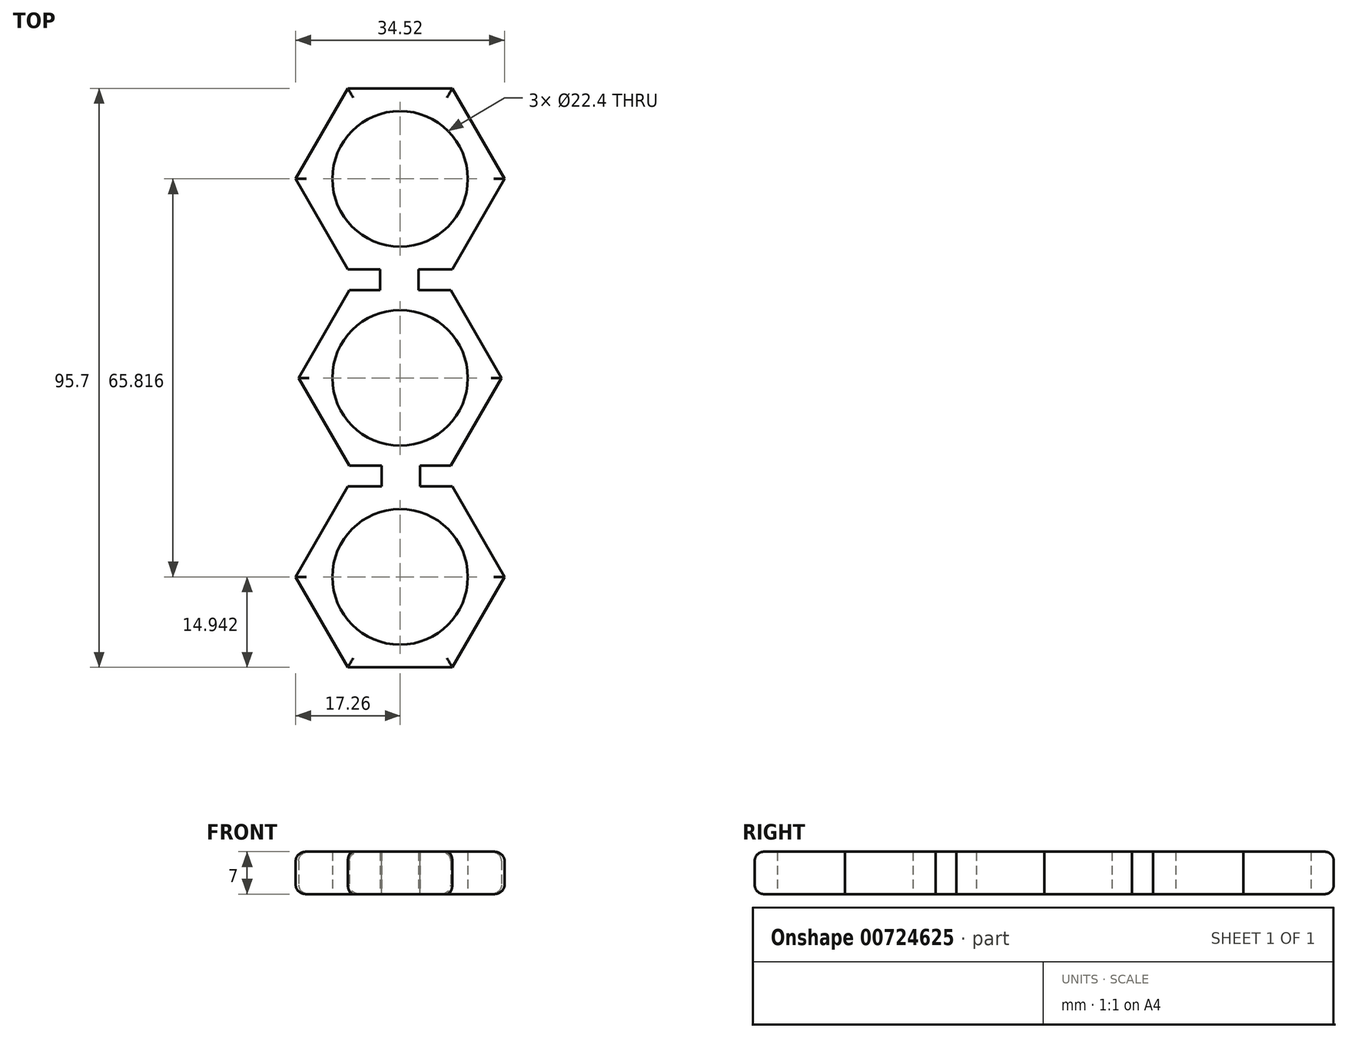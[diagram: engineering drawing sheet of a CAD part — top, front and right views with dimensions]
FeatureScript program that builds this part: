
annotation { "Feature Type Name" : "Feature", "Feature Type Description" : "" }
export const myFeature = defineFeature(function(context is Context, id is Id, definition is map)
    precondition{}
    {
        {
            var Q0;
            Q0=qCreatedBy(makeId("Top.planeOp"),FACE);
            var sketch = newSketch(context, id + "F0", { "sketchPlane" : qUnion([Q0])});
            skCircle(sketch, "E0", {"center": v(0, 0) * mm, "radius": 11.2 * mm});
            skLineSegment(sketch, "E1.0", {"start": v(8.38, -14.51) * mm, "end": v(-8.38, -14.51) * mm});
            skLineSegment(sketch, "E1.1", {"start": v(-8.38, -14.51) * mm, "end": v(-16.76, 0) * mm});
            skLineSegment(sketch, "E1.2", {"start": v(-16.76, 0) * mm, "end": v(-8.38, 14.51) * mm});
            skLineSegment(sketch, "E1.3", {"start": v(-8.38, 14.51) * mm, "end": v(8.38, 14.51) * mm});
            skLineSegment(sketch, "E1.4", {"start": v(8.38, 14.51) * mm, "end": v(16.76, 0) * mm});
            skLineSegment(sketch, "E1.5", {"start": v(16.76, 0) * mm, "end": v(8.38, -14.51) * mm});
            skPoint(sketch, "E1.0.midPoint", {"position": v(0, -14.51) * mm});
            skCircle(sketch, "E2", {"center": v(0, 32.9) * mm, "radius": 11.2 * mm});
            skLineSegment(sketch, "E3.0", {"start": v(8.63, 17.96) * mm, "end": v(-8.63, 17.96) * mm});
            skLineSegment(sketch, "E3.1", {"start": v(-8.63, 17.96) * mm, "end": v(-17.26, 32.9) * mm});
            skLineSegment(sketch, "E3.2", {"start": v(-17.26, 32.9) * mm, "end": v(-8.63, 47.85) * mm});
            skLineSegment(sketch, "E3.3", {"start": v(-8.63, 47.85) * mm, "end": v(8.63, 47.85) * mm});
            skLineSegment(sketch, "E3.4", {"start": v(8.63, 47.85) * mm, "end": v(17.26, 32.9) * mm});
            skLineSegment(sketch, "E3.5", {"start": v(17.26, 32.9) * mm, "end": v(8.63, 17.96) * mm});
            skPoint(sketch, "E3.0.midPoint", {"position": v(0, 17.96) * mm});
            skCircle(sketch, "E4.1.0", {"center": v(0, -32.9) * mm, "radius": 11.2 * mm});
            skLineSegment(sketch, "E4.1.1", {"start": v(-8.63, -47.85) * mm, "end": v(-17.26, -32.9) * mm});
            skLineSegment(sketch, "E4.1.2", {"start": v(17.26, -32.9) * mm, "end": v(8.63, -47.85) * mm});
            skLineSegment(sketch, "E4.1.3", {"start": v(8.63, -17.96) * mm, "end": v(17.26, -32.9) * mm});
            skLineSegment(sketch, "E4.1.4", {"start": v(-8.63, -17.96) * mm, "end": v(8.63, -17.96) * mm});
            skLineSegment(sketch, "E4.1.5", {"start": v(-17.26, -32.9) * mm, "end": v(-8.63, -17.96) * mm});
            skLineSegment(sketch, "E4.1.6", {"start": v(8.63, -47.85) * mm, "end": v(-8.63, -47.85) * mm});
            skLineSegment(sketch, "E5", {"start": v(-3.3, 17.96) * mm, "end": v(-3.3, 14.51) * mm});
            skLineSegment(sketch, "E6", {"start": v(3.02, 17.96) * mm, "end": v(3.02, 14.51) * mm});
            skLineSegment(sketch, "E7.1.0", {"start": v(3.3, -17.96) * mm, "end": v(3.3, -14.51) * mm});
            skLineSegment(sketch, "E7.1.1", {"start": v(-3.02, -17.96) * mm, "end": v(-3.02, -14.51) * mm});
            skSolve(sketch);
        }
        {
            var Q0;
            Q0=makeQuery(id+"F0.imprint","IMPRINT",FACE,{"disambiguationData":[TD([[makeQuery(id+"F0.imprint","IMPRINT",EDGE,{"derivedFrom":sQuery(id+"F0.wireOp",EDGE,"E2")}),-1.0]])]});
            var Q1;
            Q1=makeQuery(id+"F0.imprint","IMPRINT",FACE,{"disambiguationData":[TD([[makeQuery(id+"F0.imprint","IMPRINT",EDGE,{"derivedFrom":sQuery(id+"F0.wireOp",EDGE,"E0")}),-1.0]])]});
            var Q2;
            {var subQ0=sQuery(id+"F0.wireOp",EDGE,"E5");Q2=makeQuery(id+"F0.imprint","IMPRINT",FACE,{"disambiguationData":[TD([[makeQuery(id+"F0.imprint","IMPRINT",EDGE,{"derivedFrom":subQ0}),1.0]])]});}
            var Q3;
            Q3=makeQuery(id+"F0.imprint","IMPRINT",FACE,{"disambiguationData":[TD([[makeQuery(id+"F0.imprint","IMPRINT",EDGE,{"derivedFrom":sQuery(id+"F0.wireOp",EDGE,"E4.1.0")}),-1.0]])]});
            var Q4;
            {var subQ0=sQuery(id+"F0.wireOp",EDGE,"E7.1.0");Q4=makeQuery(id+"F0.imprint","IMPRINT",FACE,{"disambiguationData":[TD([[makeQuery(id+"F0.imprint","IMPRINT",EDGE,{"derivedFrom":subQ0}),1.0]])]});}
            extrude(context, id + "F1", {"entities" : qUnion([Q0, Q1, Q2, Q3, Q4]), "depth" : 7 * mm, "offsetDistance" : 25 * mm});
        }
        {
            var Q0;
            Q0=makeQuery(id+"F1.opExtrude","CAP_EDGE",EDGE,{"disambiguationData":[OSD([sQuery(id+"F0.wireOp",EDGE,"E3.2")])],"isStart":false});
            var Q1;
            Q1=makeQuery(id+"F1.opExtrude","CAP_EDGE",EDGE,{"disambiguationData":[OSD([sQuery(id+"F0.wireOp",EDGE,"E3.3")])],"isStart":false});
            var Q2;
            Q2=makeQuery(id+"F1.opExtrude","CAP_EDGE",EDGE,{"disambiguationData":[OSD([sQuery(id+"F0.wireOp",EDGE,"E3.4")])],"isStart":false});
            var Q3;
            Q3=makeQuery(id+"F1.opExtrude","CAP_EDGE",EDGE,{"disambiguationData":[OSD([sQuery(id+"F0.wireOp",EDGE,"E3.5")])],"isStart":false});
            var Q4;
            Q4=makeQuery(id+"F1.opExtrude","CAP_EDGE",EDGE,{"disambiguationData":[OSD([sQuery(id+"F0.wireOp",EDGE,"E3.1")])],"isStart":false});
            var Q5;
            Q5=makeQuery(id+"F1.opExtrude","CAP_EDGE",EDGE,{"disambiguationData":[OSD([sQuery(id+"F0.wireOp",EDGE,"E1.2")])],"isStart":false});
            var Q6;
            Q6=makeQuery(id+"F1.opExtrude","CAP_EDGE",EDGE,{"disambiguationData":[OSD([sQuery(id+"F0.wireOp",EDGE,"E1.5")])],"isStart":false});
            var Q7;
            Q7=makeQuery(id+"F1.opExtrude","CAP_EDGE",EDGE,{"disambiguationData":[OSD([sQuery(id+"F0.wireOp",EDGE,"E1.1")])],"isStart":false});
            var Q8;
            Q8=makeQuery(id+"F1.opExtrude","CAP_EDGE",EDGE,{"disambiguationData":[OSD([sQuery(id+"F0.wireOp",EDGE,"E4.1.5")])],"isStart":false});
            var Q9;
            Q9=makeQuery(id+"F1.opExtrude","CAP_EDGE",EDGE,{"disambiguationData":[OSD([sQuery(id+"F0.wireOp",EDGE,"E4.1.3")])],"isStart":false});
            var Q10;
            Q10=makeQuery(id+"F1.opExtrude","CAP_EDGE",EDGE,{"disambiguationData":[OSD([sQuery(id+"F0.wireOp",EDGE,"E4.1.2")])],"isStart":false});
            var Q11;
            Q11=makeQuery(id+"F1.opExtrude","CAP_EDGE",EDGE,{"disambiguationData":[OSD([sQuery(id+"F0.wireOp",EDGE,"E4.1.6")])],"isStart":false});
            var Q12;
            Q12=makeQuery(id+"F1.opExtrude","CAP_EDGE",EDGE,{"disambiguationData":[OSD([sQuery(id+"F0.wireOp",EDGE,"E4.1.1")])],"isStart":false});
            var Q13;
            Q13=makeQuery(id+"F1.opExtrude","CAP_EDGE",EDGE,{"disambiguationData":[OSD([sQuery(id+"F0.wireOp",EDGE,"E1.4")])],"isStart":false});
            var Q14;
            Q14=makeQuery(id+"F1.opExtrude","CAP_EDGE",EDGE,{"disambiguationData":[OSD([sQuery(id+"F0.wireOp",EDGE,"E4.1.1")])],"isStart":true});
            var Q15;
            Q15=makeQuery(id+"F1.opExtrude","CAP_EDGE",EDGE,{"disambiguationData":[OSD([sQuery(id+"F0.wireOp",EDGE,"E4.1.6")])],"isStart":true});
            var Q16;
            Q16=makeQuery(id+"F1.opExtrude","CAP_EDGE",EDGE,{"disambiguationData":[OSD([sQuery(id+"F0.wireOp",EDGE,"E4.1.2")])],"isStart":true});
            var Q17;
            Q17=makeQuery(id+"F1.opExtrude","CAP_EDGE",EDGE,{"disambiguationData":[OSD([sQuery(id+"F0.wireOp",EDGE,"E4.1.3")])],"isStart":true});
            var Q18;
            Q18=makeQuery(id+"F1.opExtrude","CAP_EDGE",EDGE,{"disambiguationData":[OSD([sQuery(id+"F0.wireOp",EDGE,"E4.1.5")])],"isStart":true});
            var Q19;
            Q19=makeQuery(id+"F1.opExtrude","CAP_EDGE",EDGE,{"disambiguationData":[OSD([sQuery(id+"F0.wireOp",EDGE,"E1.1")])],"isStart":true});
            var Q20;
            Q20=makeQuery(id+"F1.opExtrude","CAP_EDGE",EDGE,{"disambiguationData":[OSD([sQuery(id+"F0.wireOp",EDGE,"E1.5")])],"isStart":true});
            var Q21;
            Q21=makeQuery(id+"F1.opExtrude","CAP_EDGE",EDGE,{"disambiguationData":[OSD([sQuery(id+"F0.wireOp",EDGE,"E1.4")])],"isStart":true});
            var Q22;
            Q22=makeQuery(id+"F1.opExtrude","CAP_EDGE",EDGE,{"disambiguationData":[OSD([sQuery(id+"F0.wireOp",EDGE,"E1.2")])],"isStart":true});
            var Q23;
            Q23=makeQuery(id+"F1.opExtrude","CAP_EDGE",EDGE,{"disambiguationData":[OSD([sQuery(id+"F0.wireOp",EDGE,"E3.1")])],"isStart":true});
            var Q24;
            Q24=makeQuery(id+"F1.opExtrude","CAP_EDGE",EDGE,{"disambiguationData":[OSD([sQuery(id+"F0.wireOp",EDGE,"E3.2")])],"isStart":true});
            var Q25;
            Q25=makeQuery(id+"F1.opExtrude","CAP_EDGE",EDGE,{"disambiguationData":[OSD([sQuery(id+"F0.wireOp",EDGE,"E3.4")])],"isStart":true});
            var Q26;
            Q26=makeQuery(id+"F1.opExtrude","CAP_EDGE",EDGE,{"disambiguationData":[OSD([sQuery(id+"F0.wireOp",EDGE,"E3.3")])],"isStart":true});
            var Q27;
            Q27=makeQuery(id+"F1.opExtrude","CAP_EDGE",EDGE,{"disambiguationData":[OSD([sQuery(id+"F0.wireOp",EDGE,"E3.5")])],"isStart":true});
            fillet(context, id + "F2", {"entities" : qUnion([Q0, Q1, Q2, Q3, Q4, Q5, Q6, Q7, Q8, Q9, Q10, Q11, Q12, Q13, Q14, Q15, Q16, Q17, Q18, Q19, Q20, Q21, Q22, Q23, Q24, Q25, Q26, Q27]), "radius" : 1.5 * mm, "tangentPropagation" : true, "allowEdgeOverflow" : false});
        }
    });
